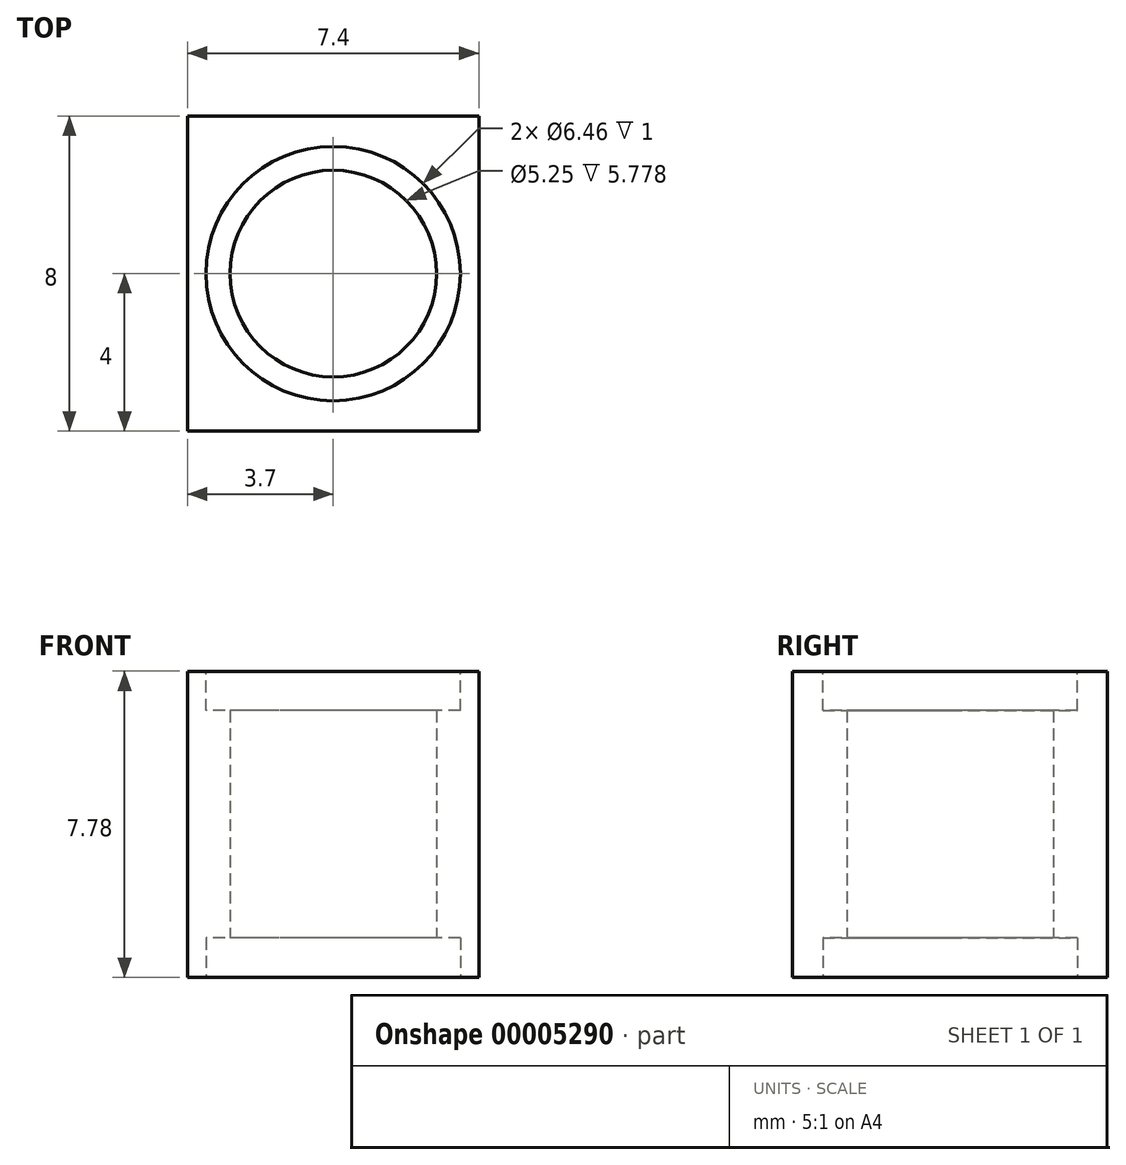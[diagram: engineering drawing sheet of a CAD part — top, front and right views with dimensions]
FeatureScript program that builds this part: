
annotation { "Feature Type Name" : "Feature", "Feature Type Description" : "" }
export const myFeature = defineFeature(function(context is Context, id is Id, definition is map)
    precondition{}
    {
        {
            var Q0;
            Q0=qCreatedBy(makeId("Top.planeOp"),FACE);
            var sketch = newSketch(context, id + "F0", { "sketchPlane" : qUnion([Q0])});
            skLineSegment(sketch, "E0.rect.bottom", {"start": v(3.7, -4) * mm, "end": v(-3.7, -4) * mm});
            skLineSegment(sketch, "E0.rect.top", {"start": v(3.7, 4) * mm, "end": v(-3.7, 4) * mm});
            skLineSegment(sketch, "E0.rect.left", {"start": v(3.7, -4) * mm, "end": v(3.7, 4) * mm});
            skLineSegment(sketch, "E0.rect.right", {"start": v(-3.7, -4) * mm, "end": v(-3.7, 4) * mm});
            skPoint(sketch, "E0.rect.middle", {"position": v(0, 0) * mm});
            skCircle(sketch, "E1", {"center": v(0, 0) * mm, "radius": 3.23 * mm});
            skCircle(sketch, "E2", {"center": v(0, 0) * mm, "radius": 2.62 * mm});
            skSolve(sketch);
        }
        {
            var Q0;
            Q0=makeQuery(id+"F0.imprint","IMPRINT",FACE,{"disambiguationData":[TD([[makeQuery(id+"F0.imprint","IMPRINT",EDGE,{"derivedFrom":sQuery(id+"F0.wireOp",EDGE,"E0.rect.bottom")}),-1.0]])]});
            var Q1;
            Q1=makeQuery(id+"F0.imprint","IMPRINT",FACE,{"disambiguationData":[TD([[makeQuery(id+"F0.imprint","IMPRINT",EDGE,{"derivedFrom":sQuery(id+"F0.wireOp",EDGE,"E1")}),1.0]])]});
            extrude(context, id + "F1", {"entities" : qUnion([Q0, Q1]), "depth" : 7.78 * mm});
        }
        {
            var Q0;
            Q0=makeQuery(id+"F1.opExtrude","CAP_FACE",FACE,{"disambiguationData":[OSD([sQuery(id+"F0.wireOp",EDGE,"E0.rect.bottom"),sQuery(id+"F0.wireOp",EDGE,"E0.rect.top"),sQuery(id+"F0.wireOp",EDGE,"E0.rect.left"),sQuery(id+"F0.wireOp",EDGE,"E0.rect.right"),sQuery(id+"F0.wireOp",EDGE,"E2")])],"isStart":false});
            var sketch = newSketch(context, id + "F2", { "sketchPlane" : qUnion([Q0])});
            skCircle(sketch, "E3.0", {"center": v(0, 0) * mm, "radius": 3.23 * mm});
            skCircle(sketch, "E4.0", {"center": v(0, 0) * mm, "radius": 2.62 * mm});
            skSolve(sketch);
        }
        {
            var Q0;
            Q0=makeQuery(id+"F2.imprint","IMPRINT",FACE,{"disambiguationData":[TD([[makeQuery(id+"F2.imprint","IMPRINT",EDGE,{"derivedFrom":sQuery(id+"F2.wireOp",EDGE,"E3.0")}),1.0]])]});
            extrude(context, id + "F3", {"entities" : qUnion([Q0]), "operationType" : NewBodyOperationType.REMOVE, "oppositeDirection" : true, "depth" : 1 * mm});
        }
        {
            var Q0;
            Q0=makeQuery(id+"F0.imprint","IMPRINT",FACE,{"disambiguationData":[TD([[makeQuery(id+"F0.imprint","IMPRINT",EDGE,{"derivedFrom":sQuery(id+"F0.wireOp",EDGE,"E1")}),1.0]])]});
            extrude(context, id + "F4", {"entities" : qUnion([Q0]), "operationType" : NewBodyOperationType.REMOVE, "depth" : 1 * mm});
        }
    });
